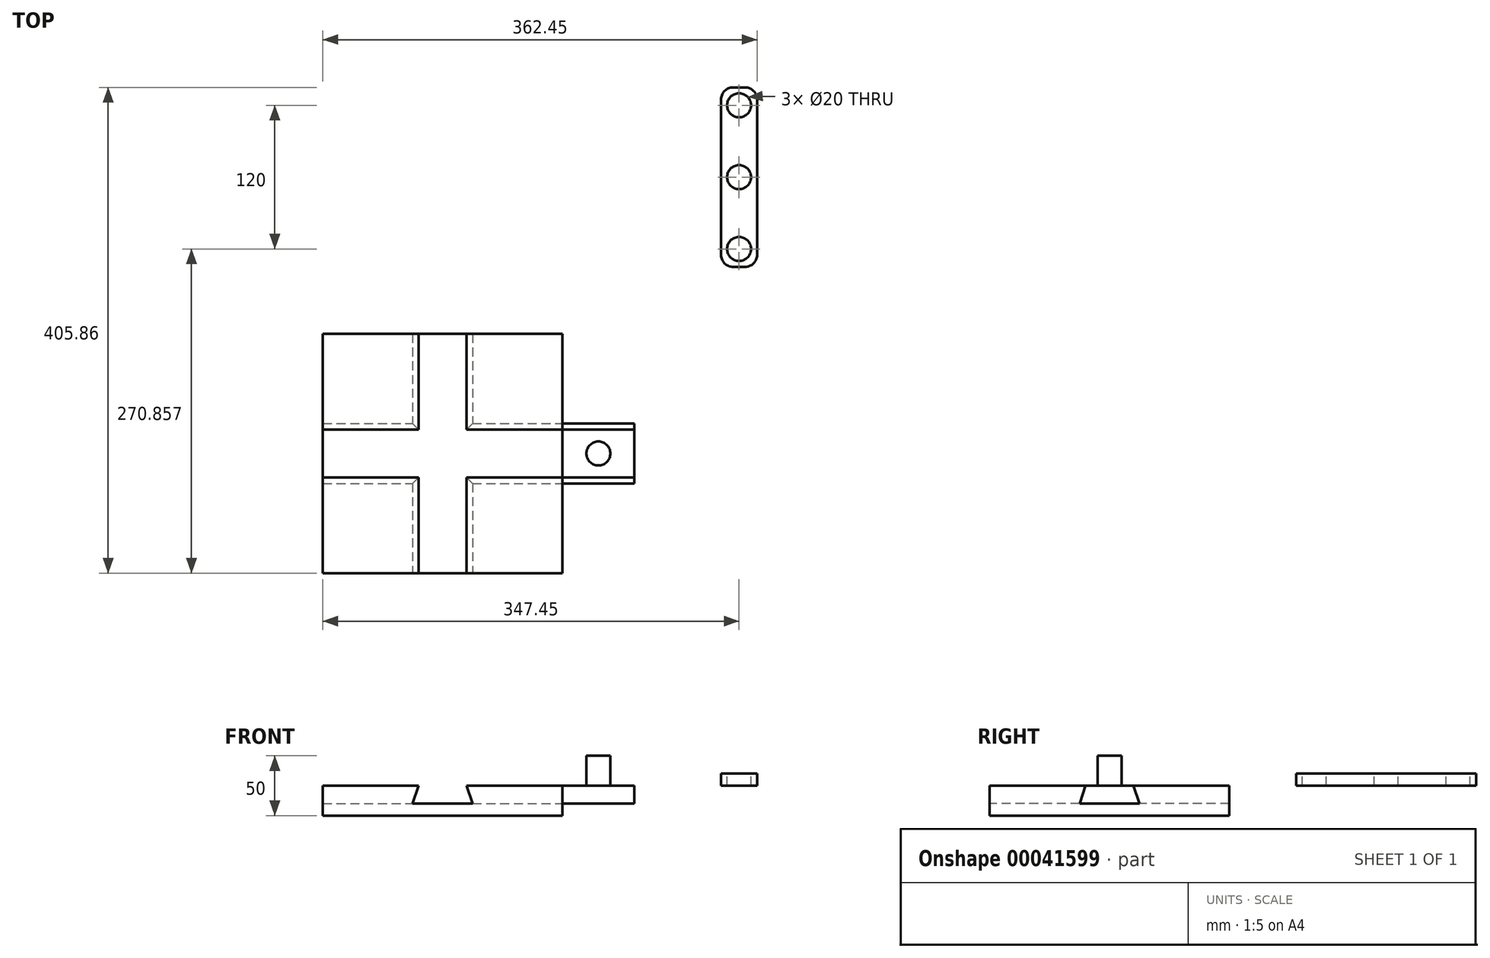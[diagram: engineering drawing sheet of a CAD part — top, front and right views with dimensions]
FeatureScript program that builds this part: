
annotation { "Feature Type Name" : "Feature", "Feature Type Description" : "" }
export const myFeature = defineFeature(function(context is Context, id is Id, definition is map)
    precondition{}
    {
        {
            var Q0;
            Q0=qCreatedBy(makeId("Top.planeOp"),FACE);
            var sketch = newSketch(context, id + "F0", { "sketchPlane" : qUnion([Q0])});
            skLineSegment(sketch, "E0.bottom", {"start": v(0, 0) * mm, "end": v(200, 0) * mm});
            skLineSegment(sketch, "E0.top", {"start": v(0, -200) * mm, "end": v(200, -200) * mm});
            skLineSegment(sketch, "E0.left", {"start": v(0, 0) * mm, "end": v(0, -200) * mm});
            skLineSegment(sketch, "E0.right", {"start": v(200, 0) * mm, "end": v(200, -200) * mm});
            skSolve(sketch);
        }
        {
            var Q0;
            Q0=makeQuery(id+"F0.imprint","IMPRINT",FACE,{"disambiguationData":[TD([[makeQuery(id+"F0.imprint","IMPRINT",EDGE,{"derivedFrom":sQuery(id+"F0.wireOp",EDGE,"E0.bottom")}),-1.0]])]});
            extrude(context, id + "F1", {"entities" : qUnion([Q0]), "depth" : 25 * mm});
        }
        {
            var Q0;
            Q0=makeQuery(id+"F1.opExtrude","SWEPT_FACE",FACE,{"disambiguationData":[OSD([sQuery(id+"F0.wireOp",EDGE,"E0.top")])]});
            var sketch = newSketch(context, id + "F2", { "sketchPlane" : qUnion([Q0])});
            skLineSegment(sketch, "E1", {"start": v(80, 25) * mm, "end": v(75, 10) * mm});
            skLineSegment(sketch, "E2", {"start": v(75, 10) * mm, "end": v(125, 10) * mm});
            skLineSegment(sketch, "E3", {"start": v(125, 10) * mm, "end": v(120, 25) * mm});
            skSolve(sketch);
        }
        {
            var Q0;
            {var subQ2=sQuery(id+"F2.wireOp",EDGE,"E1");Q0=makeQuery(id+"F2.imprint","IMPRINT",FACE,{"disambiguationData":[TD([[makeQuery(id+"F2.imprint","IMPRINT",EDGE,{"derivedFrom":subQ2}),1.0]])]});}
            extrude(context, id + "F3", {"entities" : qUnion([Q0]), "operationType" : NewBodyOperationType.REMOVE, "endBound" : BoundingType.THROUGH_ALL, "oppositeDirection" : true, "depth" : 25 * mm});
        }
        {
            var Q0;
            Q0=makeQuery(id+"F1.opExtrude","SWEPT_FACE",FACE,{"disambiguationData":[OSD([sQuery(id+"F0.wireOp",EDGE,"E0.right")])]});
            var sketch = newSketch(context, id + "F4", { "sketchPlane" : qUnion([Q0])});
            skLineSegment(sketch, "E4", {"start": v(-120, 25) * mm, "end": v(-125, 10) * mm});
            skLineSegment(sketch, "E5", {"start": v(-125, 10) * mm, "end": v(-75, 10) * mm});
            skLineSegment(sketch, "E6", {"start": v(-75, 10) * mm, "end": v(-80, 25) * mm});
            skSolve(sketch);
        }
        {
            var Q0;
            Q0 = qSketchRegion(id + "F4", true);
            var Q1;
            {var subQ2=sQuery(id+"F4.wireOp",EDGE,"E4");Q1=makeQuery(id+"F4.imprint","IMPRINT",FACE,{"disambiguationData":[TD([[makeQuery(id+"F4.imprint","IMPRINT",EDGE,{"derivedFrom":subQ2}),1.0]])]});}
            extrude(context, id + "F5", {"entities" : qUnion([Q0, Q1]), "operationType" : NewBodyOperationType.REMOVE, "endBound" : BoundingType.THROUGH_ALL, "oppositeDirection" : true, "depth" : 25 * mm});
        }
        {
            var Q0;
            {var subQ2=sQuery(id+"F4.wireOp",EDGE,"E4");Q0=makeQuery(id+"F4.imprint","IMPRINT",FACE,{"disambiguationData":[TD([[makeQuery(id+"F4.imprint","IMPRINT",EDGE,{"derivedFrom":subQ2}),1.0]])]});}
            extrude(context, id + "F6", {"entities" : qUnion([Q0]), "depth" : 60 * mm});
        }
        {
            var Q0;
            Q0=makeQuery(id+"F6.opExtrude","SWEPT_FACE",FACE,{"disambiguationData":[OSD([sQuery(id+"F0.wireOp",EDGE,"E0.right")])]});
            var sketch = newSketch(context, id + "F7", { "sketchPlane" : qUnion([Q0])});
            skCircle(sketch, "E7", {"center": v(230, -100) * mm, "radius": 10 * mm});
            skSolve(sketch);
        }
        {
            var Q0;
            Q0=makeQuery(id+"F7.imprint","IMPRINT",FACE,{"disambiguationData":[TD([[makeQuery(id+"F7.imprint","IMPRINT",EDGE,{"derivedFrom":sQuery(id+"F7.wireOp",EDGE,"E7")}),1.0]])]});
            extrude(context, id + "F8", {"entities" : qUnion([Q0]), "operationType" : NewBodyOperationType.ADD, "depth" : 25 * mm});
        }
        {
            var Q0;
            {var subQ0=sQuery(id+"F0.wireOp",EDGE,"E0.bottom");var subQ1=sQuery(id+"F0.wireOp",EDGE,"E0.top");var subQ2=sQuery(id+"F0.wireOp",EDGE,"E0.right");var subQ4=makeQuery(id+"F1.opExtrude","SWEPT_FACE",FACE,{"disambiguationData":[OSD([subQ2])]});var subQ5=makeQuery(id+"F1.opExtrude","SWEPT_FACE",FACE,{"disambiguationData":[OSD([subQ0])]});Q0=makeQuery(id+"F5.boolean.opBoolean","SPLIT",FACE,{"disambiguationData":[TD([subQ5])],"derivedFrom":makeQuery(id+"F3.boolean.opBoolean","SPLIT",FACE,{"disambiguationData":[TD([subQ4])],"derivedFrom":makeQuery(id+"F1.opExtrude","CAP_FACE",FACE,{"disambiguationData":[OSD([subQ0,subQ1,sQuery(id+"F0.wireOp",EDGE,"E0.left"),subQ2])],"isStart":false})})});}
            var sketch = newSketch(context, id + "F9", { "sketchPlane" : qUnion([Q0])});
            skLineSegment(sketch, "E8.bottom", {"start": v(332.45, 55.86) * mm, "end": v(362.45, 55.86) * mm});
            skLineSegment(sketch, "E8.top", {"start": v(332.45, 205.86) * mm, "end": v(362.45, 205.86) * mm});
            skLineSegment(sketch, "E8.left", {"start": v(332.45, 55.86) * mm, "end": v(332.45, 205.86) * mm});
            skLineSegment(sketch, "E8.right", {"start": v(362.45, 55.86) * mm, "end": v(362.45, 205.86) * mm});
            skSolve(sketch);
        }
        {
            var Q0;
            Q0 = qSketchRegion(id + "F9", true);
            extrude(context, id + "F10", {"entities" : qUnion([Q0]), "depth" : 10 * mm});
        }
        {
            var Q0;
            Q0=makeQuery(id+"F10.opExtrude","SWEPT_EDGE",EDGE,{"disambiguationData":[OSD([sQuery(id+"F9.wireOp",EDGE,"E8.bottom"),sQuery(id+"F9.wireOp",EDGE,"E8.right")])]});
            var Q1;
            Q1=makeQuery(id+"F10.opExtrude","SWEPT_EDGE",EDGE,{"disambiguationData":[OSD([sQuery(id+"F9.wireOp",EDGE,"E8.top"),sQuery(id+"F9.wireOp",EDGE,"E8.right")])]});
            var Q2;
            Q2=makeQuery(id+"F10.opExtrude","SWEPT_EDGE",EDGE,{"disambiguationData":[OSD([sQuery(id+"F9.wireOp",EDGE,"E8.top"),sQuery(id+"F9.wireOp",EDGE,"E8.left")])]});
            var Q3;
            Q3=makeQuery(id+"F10.opExtrude","SWEPT_EDGE",EDGE,{"disambiguationData":[OSD([sQuery(id+"F9.wireOp",EDGE,"E8.bottom"),sQuery(id+"F9.wireOp",EDGE,"E8.left")])]});
            fillet(context, id + "F11", {"entities" : qUnion([Q0, Q1, Q2, Q3]), "radius" : 10 * mm, "tangentPropagation" : true, "allowEdgeOverflow" : false});
        }
        {
            var Q0;
            Q0=makeQuery(id+"F10.opExtrude","CAP_FACE",FACE,{"disambiguationData":[OSD([sQuery(id+"F9.wireOp",EDGE,"E8.bottom"),sQuery(id+"F9.wireOp",EDGE,"E8.top"),sQuery(id+"F9.wireOp",EDGE,"E8.left"),sQuery(id+"F9.wireOp",EDGE,"E8.right")])],"isStart":false});
            var sketch = newSketch(context, id + "F12", { "sketchPlane" : qUnion([Q0])});
            skSolve(sketch);
        }
        {
            var Q0;
            {var subQ2=sQuery(id+"F9.wireOp",EDGE,"E8.bottom");Q0=makeQuery(id+"F12.imprint","IMPRINT",FACE,{"disambiguationData":[TD([[makeQuery(id+"F12.imprint","IMPRINT",EDGE,{"derivedFrom":makeQuery(id+"F10.opExtrude","CAP_EDGE",EDGE,{"disambiguationData":[OSD([subQ2])],"isStart":false})}),1.0]])]});}
            var sketch = newSketch(context, id + "F13", { "sketchPlane" : qUnion([Q0])});
            skCircle(sketch, "E9", {"center": v(347.45, 70.86) * mm, "radius": 10 * mm});
            skCircle(sketch, "E10", {"center": v(347.45, 130.86) * mm, "radius": 10 * mm});
            skCircle(sketch, "E11", {"center": v(347.45, 190.86) * mm, "radius": 10 * mm});
            skSolve(sketch);
        }
        {
            var Q0;
            Q0 = qSketchRegion(id + "F13", true);
            extrude(context, id + "F14", {"entities" : qUnion([Q0]), "operationType" : NewBodyOperationType.REMOVE, "endBound" : BoundingType.THROUGH_ALL, "oppositeDirection" : true, "depth" : 25 * mm});
        }
    });
